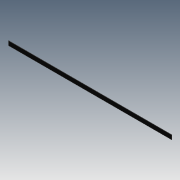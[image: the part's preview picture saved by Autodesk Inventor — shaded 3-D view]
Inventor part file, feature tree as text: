
AUTODESK INVENTOR PART (.ipt)
format: ipt  version: 2012 (Build 160160000, 160)  size: 65,536 bytes
history: native  units: in
note: dims shown in document units (in); Inventor stores cm internally (conversion verified against a paired STEP export)
features: extrude x1, sketch x1
ambient origin geometry x8: Origin, YZ Plane, XZ Plane, XY Plane, X Axis, Y Axis, Z Axis, Center Point
bodies: Solid1 (feature_tree)
feature tree (2):
  extrude  "Extrusion1"  Depth=1.0in
  sketch  "Sketch1"  dims[d0=38.5in d1=1.0in d2=0.0625in d3=0.0in]
